# Revit family: FBS4LEDS-xx-xx-xx_V1.0_Non-Hosted_R16
name_source: partatom
category: Lighting Fixtures
revit_build: Autodesk Revit 2016 (Build: 20151007_0715(x64)
units: mm (PartAtom-declared; Revit-internal decimal feet)

## family parameters
Always vertical = Yes
Cut with Voids When Loaded = No
Light Source = Yes
OmniClass Number = 23.80.70.00
OmniClass Title = Lighting
Part Type = Normal
Room Calculation Point = No
Round Connector Dimension = Use Diameter
Shared = No
Work Plane-Based = No

## types (3) — shared parameters
Color Filter = 16777215
Construction = Powder coated steel body and  PC/ABS end caps
Diffuser = Acrylic prismatic diffuser
Dimensions (L x W x H) = 1238mm x 120mm x 110mm
Dimming Lamp Color Temperature Shift = <None>
Emit Shape Visible in Rendering = No
Emit from Rectangle Length = 1219 mm
Emit from Rectangle Width = 610 mm
IP Rating = IP20
Lamp = LED strip module, 4,000K natural white, 50,000h life [L70/B50 Ta 40°C], Ra>80
Manufacturer = Clevertronics
Mounting = Surface mount
Operating Temperature = 1˚C to 40˚C
Operating Voltage = 250V AC; 50Hz
Photometric Web File = ll22575_FBS4LED-DIF-AUB04610020001.ies
Power Factor = 0.95
Replacement lamp = 8002695 PCA:LED Strip 8S6P, ALS-13-840-0-02-B
Tilt Angle = 90.00°

## per-type parameters (varying)
| type | Description | LED Driver | MIC Number | Power Consumption | Power Consumption (Standby) | Product Description | Replacement Driver | Replacement Item | Total Lumen Output |
| FBS4LED-DIF | 240V Odyssey Quantum LED diffused batten | 50W 700mA, XZ-STB50, 50,000hr | AUB04610020001 | 37 Watts |  | 240V Odyssey Quantum LED diffused batten | 1330059 LED XZ Driver - 50w 700mA, 30-54V |  | 4585 lm @ 123lm/W |
| FBS4LED-DIF-DD | 240V Odyssey Quantum LED Diffused Batten with DALI Driver | DALI Driver, 50,000h | AUB04610080001 | 39 Watts |  | 240V Odyssey Quantum LED Diffused Batten with DALI Driver | 1330056 LED Driver – LCA 50w 350-1050mA |  | 4585 lm @ 118lm/W |
| FBS4LED-DIF-MS-HL | 240V Odyssey Quantum LED diffused batten with Hi/Lo Microwave Sensor Control of the
Lamps (10%-100%) | Hytronik HED1050H/C | AUB04610090001 | 41 Watts (Standby lamps max), | 7.6 Watts (Standby lamps min) | 240V Odyssey Quantum LED diffused batten with Hi/Lo Microwave Sensor Control of the
Lamps (10%-100%) | 1330070 LED Driver - HED1050H/C, 50w | 1190118 SENSOR:Microwave Motion, IP20, MC049V | 4585 lm @ 112lm/W |

note: column(s) folded — value = type name in every type: Model

## geometry (parser evidence)
native form markers: Sweep x3
no freeform markers — native parametric forms only
